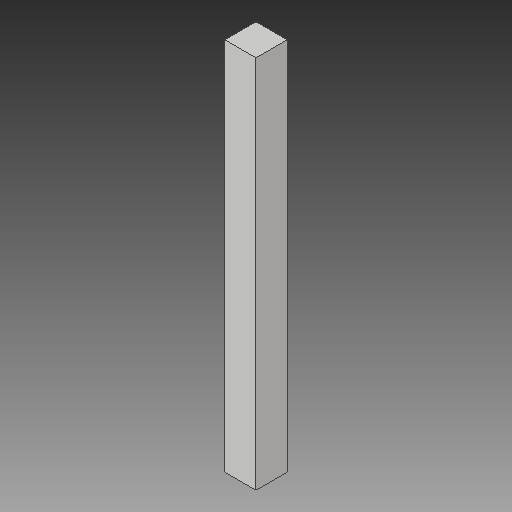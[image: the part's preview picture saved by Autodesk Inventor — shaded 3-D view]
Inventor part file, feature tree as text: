
AUTODESK INVENTOR PART (.ipt)
format: ipt  version: 2017 (Build 210142000, 142)  size: 91,136 bytes
history: native  units: in
note: dims shown in document units (in); Inventor stores cm internally (conversion verified against a paired STEP export)
features: extrude x1, sketch x1
ambient origin geometry x8: Origin, YZ Plane, XZ Plane, XY Plane, X Axis, Y Axis, Z Axis, Center Point
bodies: Solid1 (feature_tree)
feature tree (2):
  extrude  "Extrusion1"  Depth=1.0in
  sketch  "Sketch1"  dims[d0=1.0in d1=1.0in d2=12.0in d3=0.0in]
